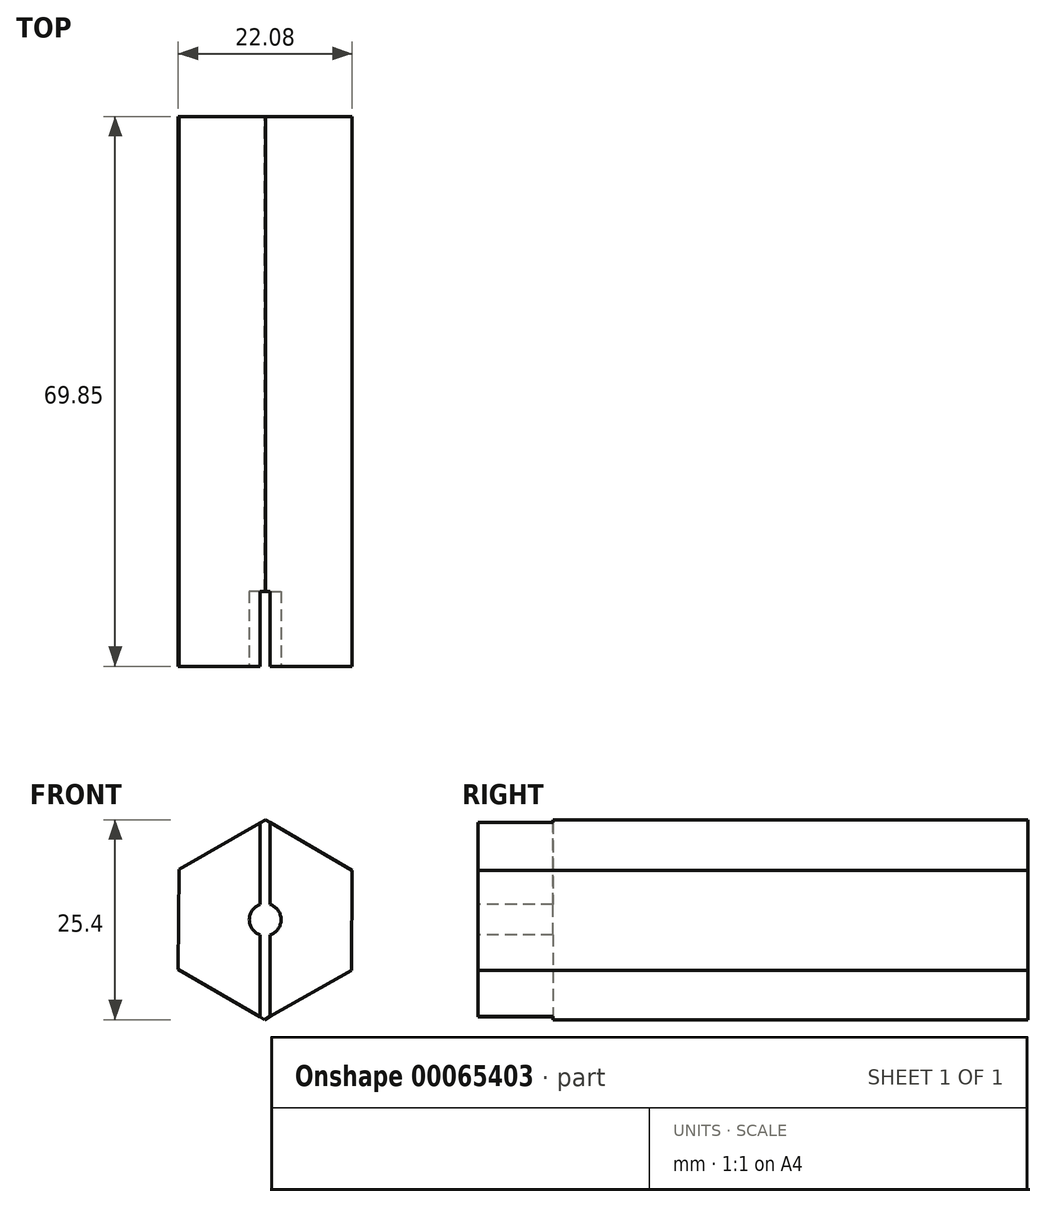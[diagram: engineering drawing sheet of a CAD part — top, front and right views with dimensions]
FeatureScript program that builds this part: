
annotation { "Feature Type Name" : "Feature", "Feature Type Description" : "" }
export const myFeature = defineFeature(function(context is Context, id is Id, definition is map)
    precondition{}
    {
        {
            var Q0;
            Q0=qCreatedBy(makeId("Front.planeOp"),FACE);
            var sketch = newSketch(context, id + "F0", { "sketchPlane" : qUnion([Q0])});
            skCircle(sketch, "E0.cCircle", {"center": v(0, 0) * mm, "radius": 11 * mm, "construction": true});
            skLineSegment(sketch, "E0.0", {"start": v(0.08, 12.7) * mm, "end": v(11.04, 6.28) * mm});
            skLineSegment(sketch, "E0.1", {"start": v(11.04, 6.28) * mm, "end": v(10.96, -6.42) * mm});
            skLineSegment(sketch, "E0.2", {"start": v(10.96, -6.42) * mm, "end": v(-0.08, -12.7) * mm});
            skLineSegment(sketch, "E0.3", {"start": v(-0.08, -12.7) * mm, "end": v(-11.04, -6.28) * mm});
            skLineSegment(sketch, "E0.4", {"start": v(-11.04, -6.28) * mm, "end": v(-10.96, 6.42) * mm});
            skLineSegment(sketch, "E0.5", {"start": v(-10.96, 6.42) * mm, "end": v(0.08, 12.7) * mm});
            skPoint(sketch, "E0.0.midPoint", {"position": v(5.56, 9.5) * mm});
            skSolve(sketch);
        }
        {
            var Q0;
            Q0=makeQuery(id+"F0.imprint","IMPRINT",FACE,{"disambiguationData":[TD([[makeQuery(id+"F0.imprint","IMPRINT",EDGE,{"derivedFrom":sQuery(id+"F0.wireOp",EDGE,"E0.0")}),-1.0]])]});
            extrude(context, id + "F1", {"entities" : qUnion([Q0]), "depth" : 69.85 * mm});
        }
        {
            var Q0;
            Q0=makeQuery(id+"F1.opExtrude","CAP_FACE",FACE,{"disambiguationData":[OSD([sQuery(id+"F0.wireOp",EDGE,"E0.0"),sQuery(id+"F0.wireOp",EDGE,"E0.1"),sQuery(id+"F0.wireOp",EDGE,"E0.2"),sQuery(id+"F0.wireOp",EDGE,"E0.3"),sQuery(id+"F0.wireOp",EDGE,"E0.4"),sQuery(id+"F0.wireOp",EDGE,"E0.5")])],"isStart":false});
            var sketch = newSketch(context, id + "F2", { "sketchPlane" : qUnion([Q0])});
            skLineSegment(sketch, "E1", {"start": v(-0.64, 0) * mm, "end": v(-0.64, -12.37) * mm});
            skLineSegment(sketch, "E2", {"start": v(-0.64, -12.37) * mm, "end": v(-0.64, 12.3) * mm});
            skLineSegment(sketch, "E3", {"start": v(0.63, 0) * mm, "end": v(0.63, -12.3) * mm});
            skLineSegment(sketch, "E4", {"start": v(0.63, -12.3) * mm, "end": v(0.63, 12.37) * mm});
            skLineSegment(sketch, "E5", {"start": v(0.63, 12.37) * mm, "end": v(0.08, 12.7) * mm});
            skLineSegment(sketch, "E6", {"start": v(0.08, 12.7) * mm, "end": v(-0.64, 12.3) * mm});
            skLineSegment(sketch, "E7", {"start": v(-0.64, -12.37) * mm, "end": v(-0.08, -12.7) * mm});
            skLineSegment(sketch, "E8", {"start": v(-0.08, -12.7) * mm, "end": v(0.63, -12.3) * mm});
            skSolve(sketch);
        }
        {
            var Q0;
            {var subQ0=sQuery(id+"F2.wireOp",EDGE,"E5");Q0=makeQuery(id+"F2.imprint","IMPRINT",FACE,{"disambiguationData":[TD([[makeQuery(id+"F2.imprint","IMPRINT",EDGE,{"derivedFrom":subQ0}),-1.0]])]});}
            extrude(context, id + "F3", {"entities" : qUnion([Q0]), "operationType" : NewBodyOperationType.REMOVE, "oppositeDirection" : true, "depth" : 9.52 * mm});
        }
        {
            var Q0;
            {var subQ0=sQuery(id+"F0.wireOp",EDGE,"E0.0");var subQ1=sQuery(id+"F0.wireOp",EDGE,"E0.1");var subQ2=sQuery(id+"F0.wireOp",EDGE,"E0.2");Q0=makeQuery(id+"F3.boolean.opBoolean","SPLIT",FACE,{"disambiguationData":[TD([makeQuery(id+"F1.opExtrude","SWEPT_FACE",FACE,{"disambiguationData":[OSD([subQ0])]})])],"derivedFrom":makeQuery(id+"F1.opExtrude","CAP_FACE",FACE,{"disambiguationData":[OSD([subQ0,subQ1,subQ2,sQuery(id+"F0.wireOp",EDGE,"E0.3"),sQuery(id+"F0.wireOp",EDGE,"E0.4"),sQuery(id+"F0.wireOp",EDGE,"E0.5")])],"isStart":false})});}
            var sketch = newSketch(context, id + "F4", { "sketchPlane" : qUnion([Q0])});
            skCircle(sketch, "E9", {"center": v(0, 0) * mm, "radius": 2.02 * mm});
            skSolve(sketch);
        }
        {
            var Q0;
            {var subQ0=sQuery(id+"F4.wireOp",EDGE,"E9");var subQ1=makeQuery(id+"F3.boolean.opBoolean","COPY",EDGE,{"derivedFrom":makeQuery(id+"F3.opExtrude","CAP_EDGE",EDGE,{"disambiguationData":[OSD([sQuery(id+"F2.wireOp",EDGE,"E4")])],"isStart":true})});var subQ2=makeQuery(id+"F4.imprint","INTERSECT",VERTEX,{"disambiguationData":[OD(0.0)],"derivedFrom":[subQ1,subQ0]});Q0=makeQuery(id+"F4.imprint","IMPRINT",FACE,{"disambiguationData":[TD([[makeQuery(id+"F4.imprint","IMPRINT",EDGE,{"disambiguationData":[TD([[subQ2,-1.0]])],"derivedFrom":subQ0}),1.0]])]});}
            var Q1;
            {var subQ0=sQuery(id+"F4.wireOp",EDGE,"E9");var subQ1=makeQuery(id+"F3.boolean.opBoolean","COPY",EDGE,{"derivedFrom":makeQuery(id+"F3.opExtrude","CAP_EDGE",EDGE,{"disambiguationData":[OSD([sQuery(id+"F2.wireOp",EDGE,"E4")])],"isStart":true})});var subQ2=makeQuery(id+"F4.imprint","INTERSECT",VERTEX,{"disambiguationData":[OD(0.0)],"derivedFrom":[subQ1,subQ0]});Q1=makeQuery(id+"F4.imprint","IMPRINT",FACE,{"disambiguationData":[TD([[makeQuery(id+"F4.imprint","IMPRINT",EDGE,{"disambiguationData":[TD([[subQ2,1.0]])],"derivedFrom":subQ0}),1.0]])]});}
            extrude(context, id + "F5", {"entities" : qUnion([Q0, Q1]), "operationType" : NewBodyOperationType.REMOVE, "oppositeDirection" : true, "depth" : 9.52 * mm});
        }
    });
